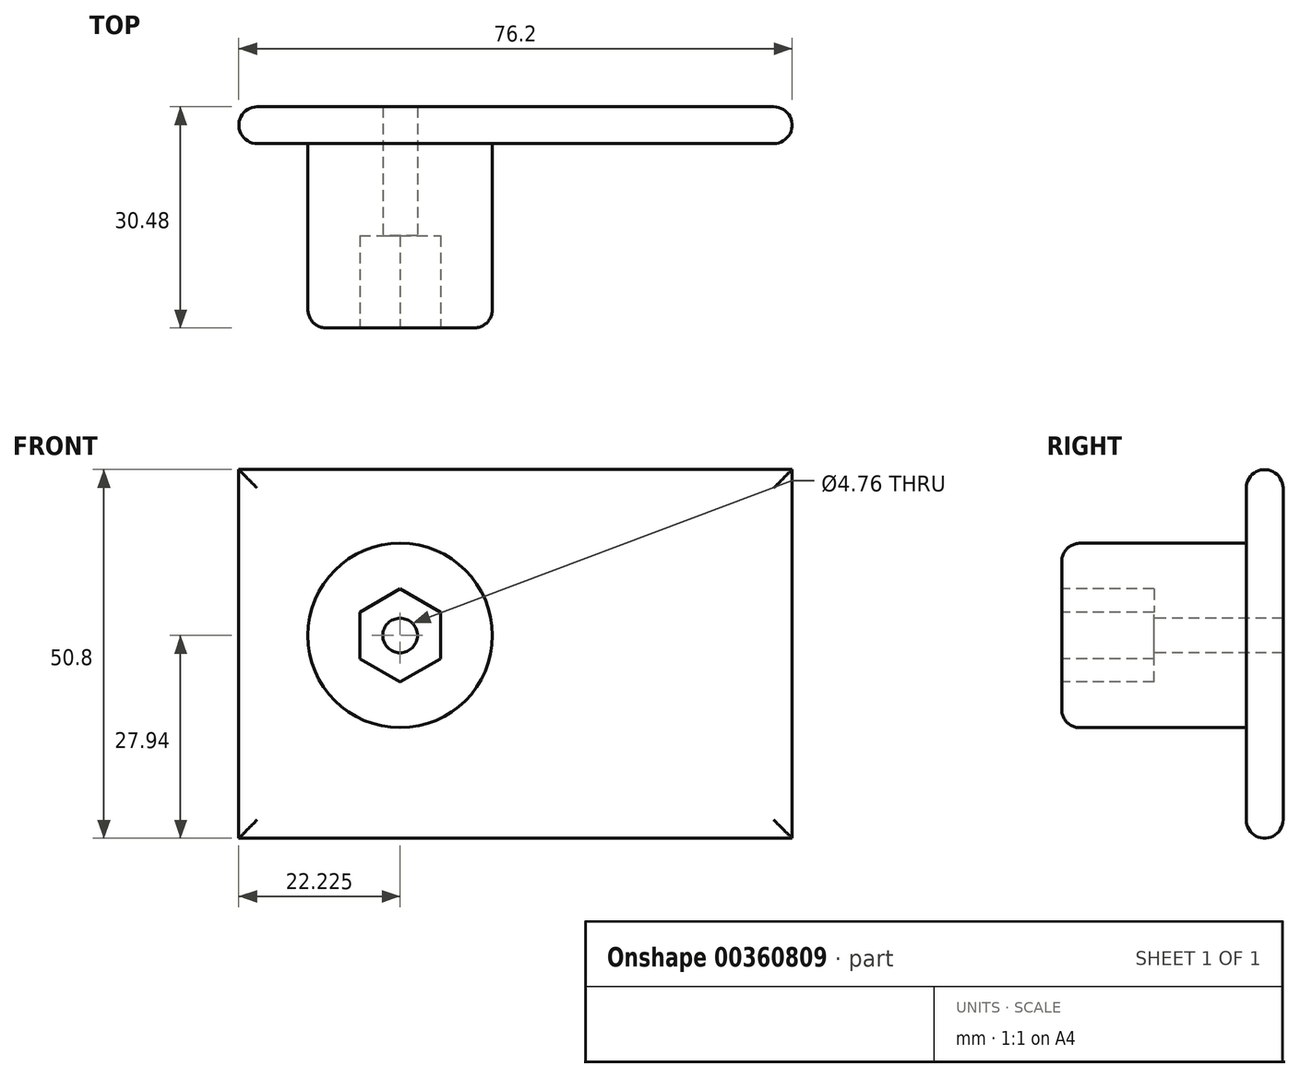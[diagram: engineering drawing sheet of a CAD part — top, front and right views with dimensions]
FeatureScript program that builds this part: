
annotation { "Feature Type Name" : "Feature", "Feature Type Description" : "" }
export const myFeature = defineFeature(function(context is Context, id is Id, definition is map)
    precondition{}
    {
        {
            var Q0;
            Q0=qCreatedBy(makeId("Front.planeOp"),FACE);
            var sketch = newSketch(context, id + "F0", { "sketchPlane" : qUnion([Q0])});
            skLineSegment(sketch, "E0.bottom", {"start": v(38.1, 25.4) * mm, "end": v(-38.1, 25.4) * mm});
            skLineSegment(sketch, "E0.top", {"start": v(38.1, -25.4) * mm, "end": v(-38.1, -25.4) * mm});
            skLineSegment(sketch, "E0.left", {"start": v(38.1, 25.4) * mm, "end": v(38.1, -25.4) * mm});
            skLineSegment(sketch, "E0.right", {"start": v(-38.1, 25.4) * mm, "end": v(-38.1, -25.4) * mm});
            skPoint(sketch, "E0.middle", {"position": v(0, 0) * mm});
            skSolve(sketch);
        }
        {
            var Q0;
            Q0 = qSketchRegion(id + "F0", true);
            extrude(context, id + "F1", {"entities" : qUnion([Q0]), "depth" : 5.08 * mm});
        }
        {
            var Q0;
            Q0=makeQuery(id+"F1.opExtrude","CAP_FACE",FACE,{"disambiguationData":[OSD([sQuery(id+"F0.wireOp",EDGE,"E0.bottom"),sQuery(id+"F0.wireOp",EDGE,"E0.top"),sQuery(id+"F0.wireOp",EDGE,"E0.left"),sQuery(id+"F0.wireOp",EDGE,"E0.right")])],"isStart":false});
            var sketch = newSketch(context, id + "F2", { "sketchPlane" : qUnion([Q0])});
            skCircle(sketch, "E1", {"center": v(-15.88, 2.54) * mm, "radius": 12.7 * mm});
            skSolve(sketch);
        }
        {
            var Q0;
            Q0 = qSketchRegion(id + "F2", true);
            extrude(context, id + "F3", {"entities" : qUnion([Q0]), "operationType" : NewBodyOperationType.ADD, "depth" : 25.4 * mm});
        }
        {
            var Q0;
            Q0=makeQuery(id+"F3.opExtrude","CAP_FACE",FACE,{"disambiguationData":[OSD([sQuery(id+"F2.wireOp",EDGE,"E1")])],"isStart":false});
            var sketch = newSketch(context, id + "F4", { "sketchPlane" : qUnion([Q0])});
            skCircle(sketch, "E2.cCircle", {"center": v(-15.88, 2.54) * mm, "radius": 5.56 * mm, "construction": true});
            skLineSegment(sketch, "E2.0", {"start": v(-15.88, 8.96) * mm, "end": v(-10.32, 5.75) * mm});
            skLineSegment(sketch, "E2.1", {"start": v(-10.32, 5.75) * mm, "end": v(-10.32, -0.67) * mm});
            skLineSegment(sketch, "E2.2", {"start": v(-10.32, -0.67) * mm, "end": v(-15.88, -3.88) * mm});
            skLineSegment(sketch, "E2.3", {"start": v(-15.88, -3.88) * mm, "end": v(-21.43, -0.67) * mm});
            skLineSegment(sketch, "E2.4", {"start": v(-21.43, -0.67) * mm, "end": v(-21.43, 5.75) * mm});
            skLineSegment(sketch, "E2.5", {"start": v(-21.43, 5.75) * mm, "end": v(-15.88, 8.96) * mm});
            skPoint(sketch, "E2.0.midPoint", {"position": v(-13.1, 7.35) * mm});
            skSolve(sketch);
        }
        {
            var Q0;
            Q0 = qSketchRegion(id + "F4", true);
            extrude(context, id + "F5", {"entities" : qUnion([Q0]), "operationType" : NewBodyOperationType.REMOVE, "oppositeDirection" : true, "depth" : 12.7 * mm});
        }
        {
            var Q0;
            Q0=makeQuery(id+"F5.boolean.opBoolean","COPY",FACE,{"derivedFrom":makeQuery(id+"F5.opExtrude","CAP_FACE",FACE,{"disambiguationData":[OSD([sQuery(id+"F4.wireOp",EDGE,"E2.0"),sQuery(id+"F4.wireOp",EDGE,"E2.1"),sQuery(id+"F4.wireOp",EDGE,"E2.2"),sQuery(id+"F4.wireOp",EDGE,"E2.3"),sQuery(id+"F4.wireOp",EDGE,"E2.4"),sQuery(id+"F4.wireOp",EDGE,"E2.5")])],"isStart":false})});
            var sketch = newSketch(context, id + "F6", { "sketchPlane" : qUnion([Q0])});
            skCircle(sketch, "E3", {"center": v(-15.88, 2.54) * mm, "radius": 2.38 * mm});
            skPoint(sketch, "E3.centerSnap0", {"position": v(-21.43, 2.54) * mm});
            skLineSegment(sketch, "E4", {"start": v(-21.43, 5.75) * mm, "end": v(-10.32, -0.67) * mm, "construction": true});
            skSolve(sketch);
        }
        {
            var Q0;
            Q0 = qSketchRegion(id + "F6", true);
            extrude(context, id + "F7", {"entities" : qUnion([Q0]), "operationType" : NewBodyOperationType.REMOVE, "endBound" : BoundingType.UP_TO_NEXT, "oppositeDirection" : true, "depth" : 25.4 * mm});
        }
        {
            var Q0;
            Q0=makeQuery(id+"F3.opExtrude","CAP_EDGE",EDGE,{"disambiguationData":[OSD([sQuery(id+"F2.wireOp",EDGE,"E1")])],"isStart":false});
            var Q1;
            Q1=makeQuery(id+"F3.opExtrude","CAP_EDGE",EDGE,{"disambiguationData":[OSD([sQuery(id+"F2.wireOp",EDGE,"E1")])],"isStart":true});
            var Q2;
            Q2=makeQuery(id+"F1.opExtrude","CAP_EDGE",EDGE,{"disambiguationData":[OSD([sQuery(id+"F0.wireOp",EDGE,"E0.bottom")])],"isStart":false});
            var Q3;
            Q3=makeQuery(id+"F1.opExtrude","CAP_EDGE",EDGE,{"disambiguationData":[OSD([sQuery(id+"F0.wireOp",EDGE,"E0.left")])],"isStart":false});
            var Q4;
            Q4=makeQuery(id+"F1.opExtrude","CAP_EDGE",EDGE,{"disambiguationData":[OSD([sQuery(id+"F0.wireOp",EDGE,"E0.top")])],"isStart":false});
            var Q5;
            Q5=makeQuery(id+"F1.opExtrude","CAP_EDGE",EDGE,{"disambiguationData":[OSD([sQuery(id+"F0.wireOp",EDGE,"E0.right")])],"isStart":false});
            var Q6;
            Q6=makeQuery(id+"F1.opExtrude","CAP_EDGE",EDGE,{"disambiguationData":[OSD([sQuery(id+"F0.wireOp",EDGE,"E0.top")])],"isStart":true});
            var Q7;
            Q7=makeQuery(id+"F1.opExtrude","CAP_EDGE",EDGE,{"disambiguationData":[OSD([sQuery(id+"F0.wireOp",EDGE,"E0.right")])],"isStart":true});
            var Q8;
            Q8=makeQuery(id+"F1.opExtrude","CAP_EDGE",EDGE,{"disambiguationData":[OSD([sQuery(id+"F0.wireOp",EDGE,"E0.left")])],"isStart":true});
            var Q9;
            Q9=makeQuery(id+"F1.opExtrude","CAP_EDGE",EDGE,{"disambiguationData":[OSD([sQuery(id+"F0.wireOp",EDGE,"E0.bottom")])],"isStart":true});
            fillet(context, id + "F8", {"entities" : qUnion([Q0, Q1, Q2, Q3, Q4, Q5, Q6, Q7, Q8, Q9]), "radius" : 2.54 * mm, "tangentPropagation" : true, "allowEdgeOverflow" : false});
        }
    });
